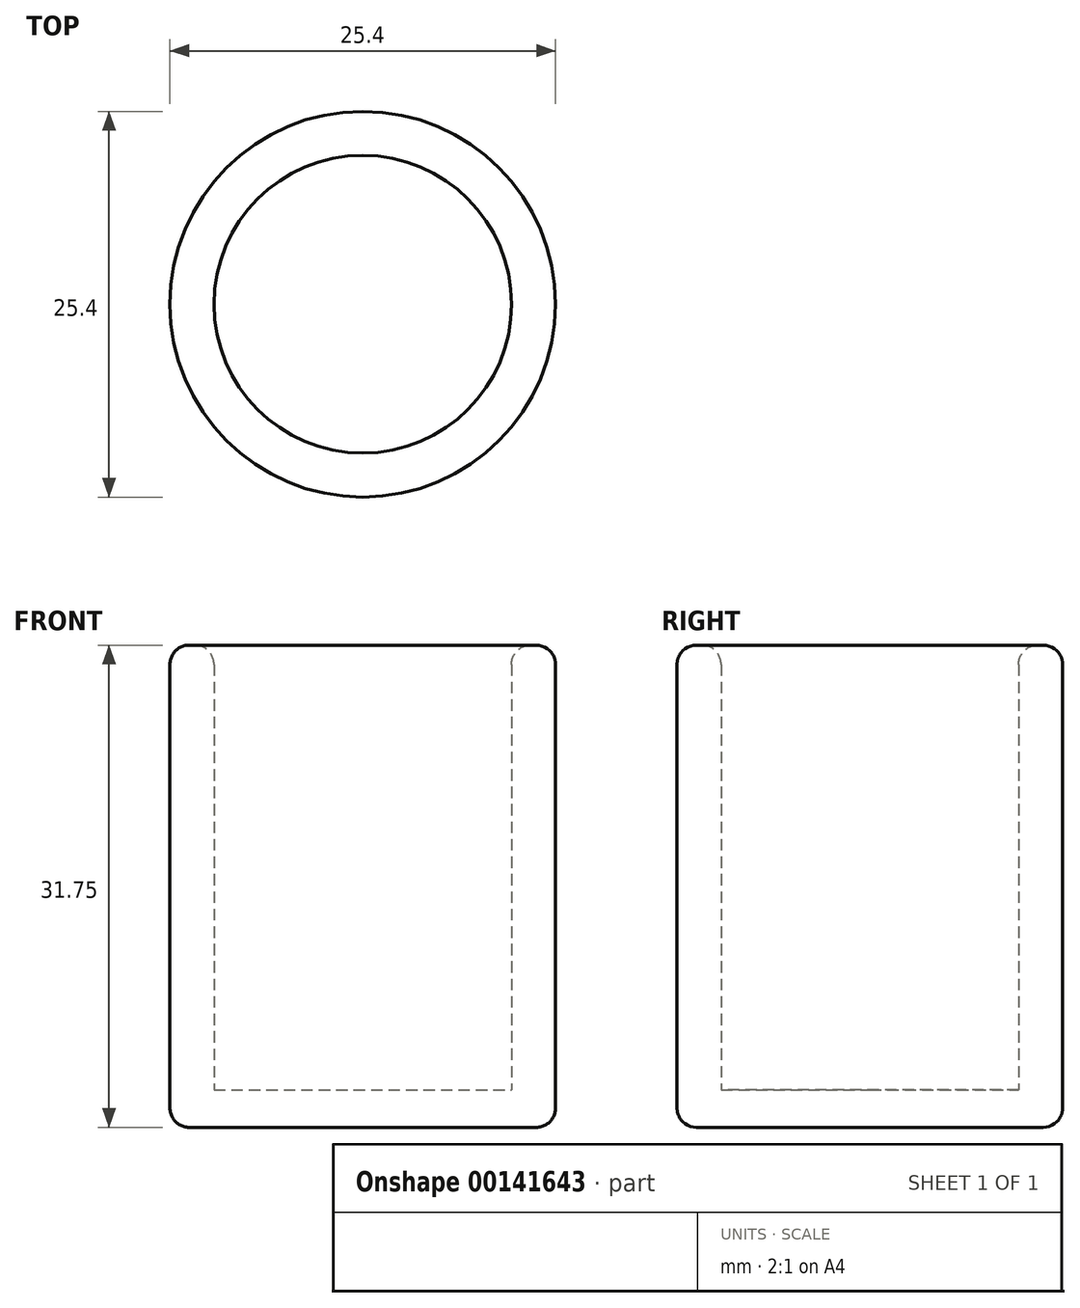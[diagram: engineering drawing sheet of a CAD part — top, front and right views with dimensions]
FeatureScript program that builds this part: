
annotation { "Feature Type Name" : "Feature", "Feature Type Description" : "" }
export const myFeature = defineFeature(function(context is Context, id is Id, definition is map)
    precondition{}
    {
        {
            var Q0;
            Q0=qCreatedBy(makeId("Front.planeOp"),FACE);
            var sketch = newSketch(context, id + "F0", { "sketchPlane" : qUnion([Q0])});
            skLineSegment(sketch, "E0", {"start": v(-12.7, 0) * mm, "end": v(0, 0) * mm});
            skLineSegment(sketch, "E1", {"start": v(0, 0) * mm, "end": v(0, 2.46) * mm});
            skLineSegment(sketch, "E2", {"start": v(0, 2.46) * mm, "end": v(-9.8, 2.46) * mm});
            skLineSegment(sketch, "E3", {"start": v(-9.8, 2.46) * mm, "end": v(-9.8, 31.75) * mm});
            skLineSegment(sketch, "E4", {"start": v(-9.8, 31.75) * mm, "end": v(-12.7, 31.75) * mm});
            skLineSegment(sketch, "E5", {"start": v(-12.7, 31.75) * mm, "end": v(-12.7, 0) * mm});
            skSolve(sketch);
        }
        {
            var Q0;
            Q0=makeQuery(id+"F0.imprint","IMPRINT",FACE,{"disambiguationData":[TD([[makeQuery(id+"F0.imprint","IMPRINT",EDGE,{"derivedFrom":sQuery(id+"F0.wireOp",EDGE,"E0")}),1.0]])]});
            var Q1;
            Q1=sQuery(id+"F0.wireOp",EDGE,"E1");
            revolve(context, id + "F1", {"entities" : qUnion([Q0]), "axis" : qUnion([Q1]), "revolveType" : RevolveType.FULL});
        }
        {
            var Q0;
            Q0=makeQuery(id+"F1.opRevolve","SWEPT_EDGE",EDGE,{"disambiguationData":[OSD([sQuery(id+"F0.wireOp",EDGE,"E4"),sQuery(id+"F0.wireOp",EDGE,"E5")])]});
            var Q1;
            Q1=makeQuery(id+"F1.opRevolve","SWEPT_EDGE",EDGE,{"disambiguationData":[OSD([sQuery(id+"F0.wireOp",EDGE,"E3"),sQuery(id+"F0.wireOp",EDGE,"E4")])]});
            var Q2;
            Q2=makeQuery(id+"F1.opRevolve","SWEPT_EDGE",EDGE,{"disambiguationData":[OSD([sQuery(id+"F0.wireOp",EDGE,"E0"),sQuery(id+"F0.wireOp",EDGE,"E5")])]});
            fillet(context, id + "F2", {"entities" : qUnion([Q0, Q1, Q2]), "radius" : 1.27 * mm, "tangentPropagation" : true, "allowEdgeOverflow" : false});
        }
    });
